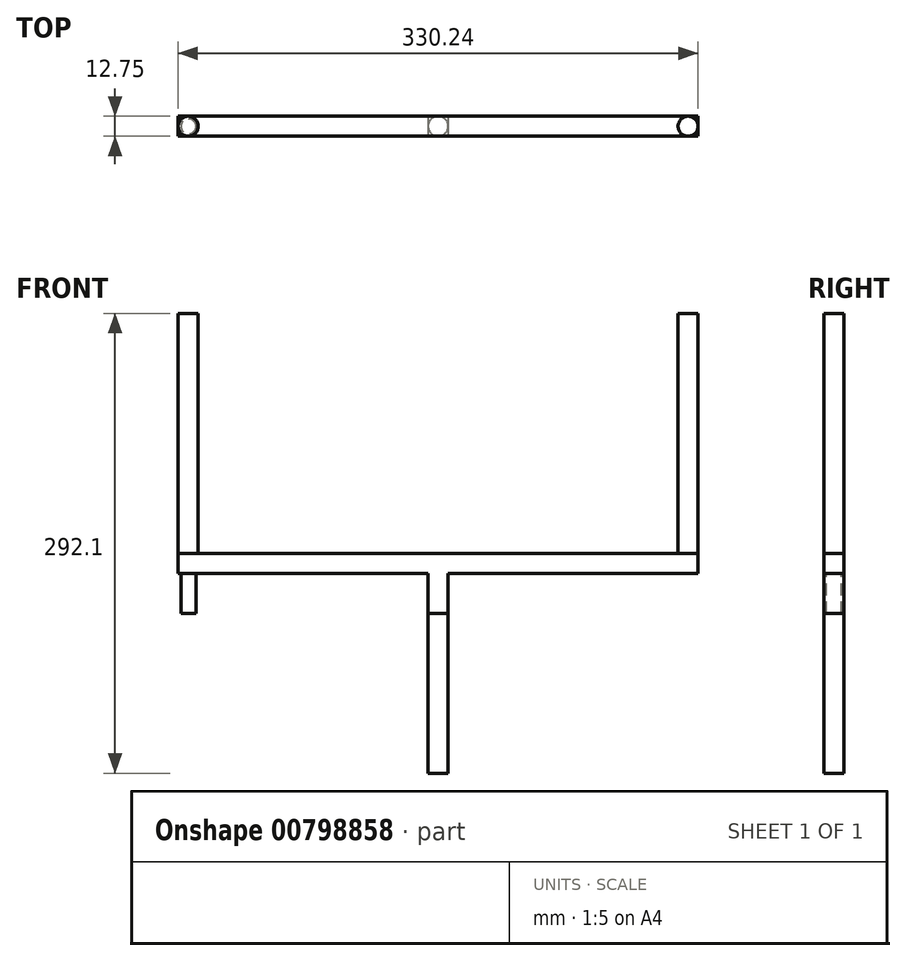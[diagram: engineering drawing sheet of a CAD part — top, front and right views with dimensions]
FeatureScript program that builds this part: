
annotation { "Feature Type Name" : "Feature", "Feature Type Description" : "" }
export const myFeature = defineFeature(function(context is Context, id is Id, definition is map)
    precondition{}
    {
        {
            var Q0;
            Q0=qCreatedBy(makeId("Top.planeOp"),FACE);
            var sketch = newSketch(context, id + "F0", { "sketchPlane" : qUnion([Q0])});
            skCircle(sketch, "E0", {"center": v(261.66, 23.91) * mm, "radius": 6.35 * mm});
            skCircle(sketch, "E1", {"center": v(-55.84, 23.91) * mm, "radius": 6.35 * mm});
            skSolve(sketch);
        }
        {
            var Q0;
            Q0 = qSketchRegion(id + "F0", true);
            extrude(context, id + "F1", {"entities" : qUnion([Q0]), "depth" : 152.4 * mm, "offsetDistance" : 25.4 * mm});
        }
        {
            var Q0;
            Q0=makeQuery(id+"F1.opExtrude","CAP_FACE",FACE,{"disambiguationData":[OSD([sQuery(id+"F0.wireOp",EDGE,"E1")])],"isStart":true});
            var sketch = newSketch(context, id + "F2", { "sketchPlane" : qUnion([Q0])});
            skLineSegment(sketch, "E2.bottom", {"start": v(-62.15, -17.61) * mm, "end": v(268.05, -17.61) * mm});
            skLineSegment(sketch, "E2.top", {"start": v(-62.15, -30.31) * mm, "end": v(268.05, -30.31) * mm});
            skLineSegment(sketch, "E2.left", {"start": v(-62.15, -17.61) * mm, "end": v(-62.15, -30.31) * mm});
            skLineSegment(sketch, "E2.right", {"start": v(268.05, -17.61) * mm, "end": v(268.05, -30.31) * mm});
            skSolve(sketch);
        }
        {
            var Q0;
            Q0 = qSketchRegion(id + "F2", true);
            extrude(context, id + "F3", {"entities" : qUnion([Q0]), "depth" : 12.7 * mm, "offsetDistance" : 25.4 * mm});
        }
        {
            var Q0;
            Q0=makeQuery(id+"F3.opExtrude","CAP_FACE",FACE,{"disambiguationData":[OSD([sQuery(id+"F2.wireOp",EDGE,"E2.bottom"),sQuery(id+"F2.wireOp",EDGE,"E2.top"),sQuery(id+"F2.wireOp",EDGE,"E2.left"),sQuery(id+"F2.wireOp",EDGE,"E2.right")])],"isStart":false});
            var sketch = newSketch(context, id + "F4", { "sketchPlane" : qUnion([Q0])});
            skLineSegment(sketch, "E3.bottom", {"start": v(109.3, -30.31) * mm, "end": v(96.6, -30.31) * mm});
            skLineSegment(sketch, "E3.top", {"start": v(109.3, -17.61) * mm, "end": v(96.6, -17.61) * mm});
            skLineSegment(sketch, "E3.left", {"start": v(109.3, -30.31) * mm, "end": v(109.3, -17.61) * mm});
            skLineSegment(sketch, "E3.right", {"start": v(96.6, -30.31) * mm, "end": v(96.6, -17.61) * mm});
            skPoint(sketch, "E3.middle", {"position": v(102.95, -23.96) * mm});
            skSolve(sketch);
        }
        {
            var Q0;
            Q0=makeQuery(id+"F3.opExtrude","CAP_FACE",FACE,{"disambiguationData":[OSD([sQuery(id+"F2.wireOp",EDGE,"E2.bottom"),sQuery(id+"F2.wireOp",EDGE,"E2.top"),sQuery(id+"F2.wireOp",EDGE,"E2.left"),sQuery(id+"F2.wireOp",EDGE,"E2.right")])],"isStart":false});
            var sketch = newSketch(context, id + "F5", { "sketchPlane" : qUnion([Q0])});
            skCircle(sketch, "E4", {"center": v(-55.62, -23.9) * mm, "radius": 4.76 * mm});
            skSolve(sketch);
        }
        {
            var Q0;
            Q0 = qSketchRegion(id + "F5", true);
            extrude(context, id + "F6", {"entities" : qUnion([Q0]), "operationType" : NewBodyOperationType.ADD, "depth" : 25.4 * mm, "offsetDistance" : 25.4 * mm});
        }
        {
            var Q0;
            Q0 = qSketchRegion(id + "F4", true);
            extrude(context, id + "F7", {"entities" : qUnion([Q0]), "operationType" : NewBodyOperationType.ADD, "depth" : 25.4 * mm, "offsetDistance" : 25.4 * mm});
        }
        {
            var Q0;
            Q0=makeQuery(id+"F7.opExtrude","CAP_FACE",FACE,{"disambiguationData":[OSD([sQuery(id+"F4.wireOp",EDGE,"E3.bottom"),sQuery(id+"F4.wireOp",EDGE,"E3.top"),sQuery(id+"F4.wireOp",EDGE,"E3.left"),sQuery(id+"F4.wireOp",EDGE,"E3.right")])],"isStart":false});
            var sketch = newSketch(context, id + "F8", { "sketchPlane" : qUnion([Q0])});
            skCircle(sketch, "E5", {"center": v(102.95, -23.96) * mm, "radius": 6.35 * mm});
            skPoint(sketch, "E5.first.point", {"position": v(96.6, -23.96) * mm});
            skPoint(sketch, "E5.second.point", {"position": v(109.3, -23.96) * mm});
            skPoint(sketch, "E5.third.point", {"position": v(102.95, -17.61) * mm});
            skSolve(sketch);
        }
        {
            var Q0;
            Q0 = qSketchRegion(id + "F8", true);
            extrude(context, id + "F9", {"entities" : qUnion([Q0]), "operationType" : NewBodyOperationType.ADD, "depth" : 101.6 * mm, "offsetDistance" : 25.4 * mm});
        }
    });
